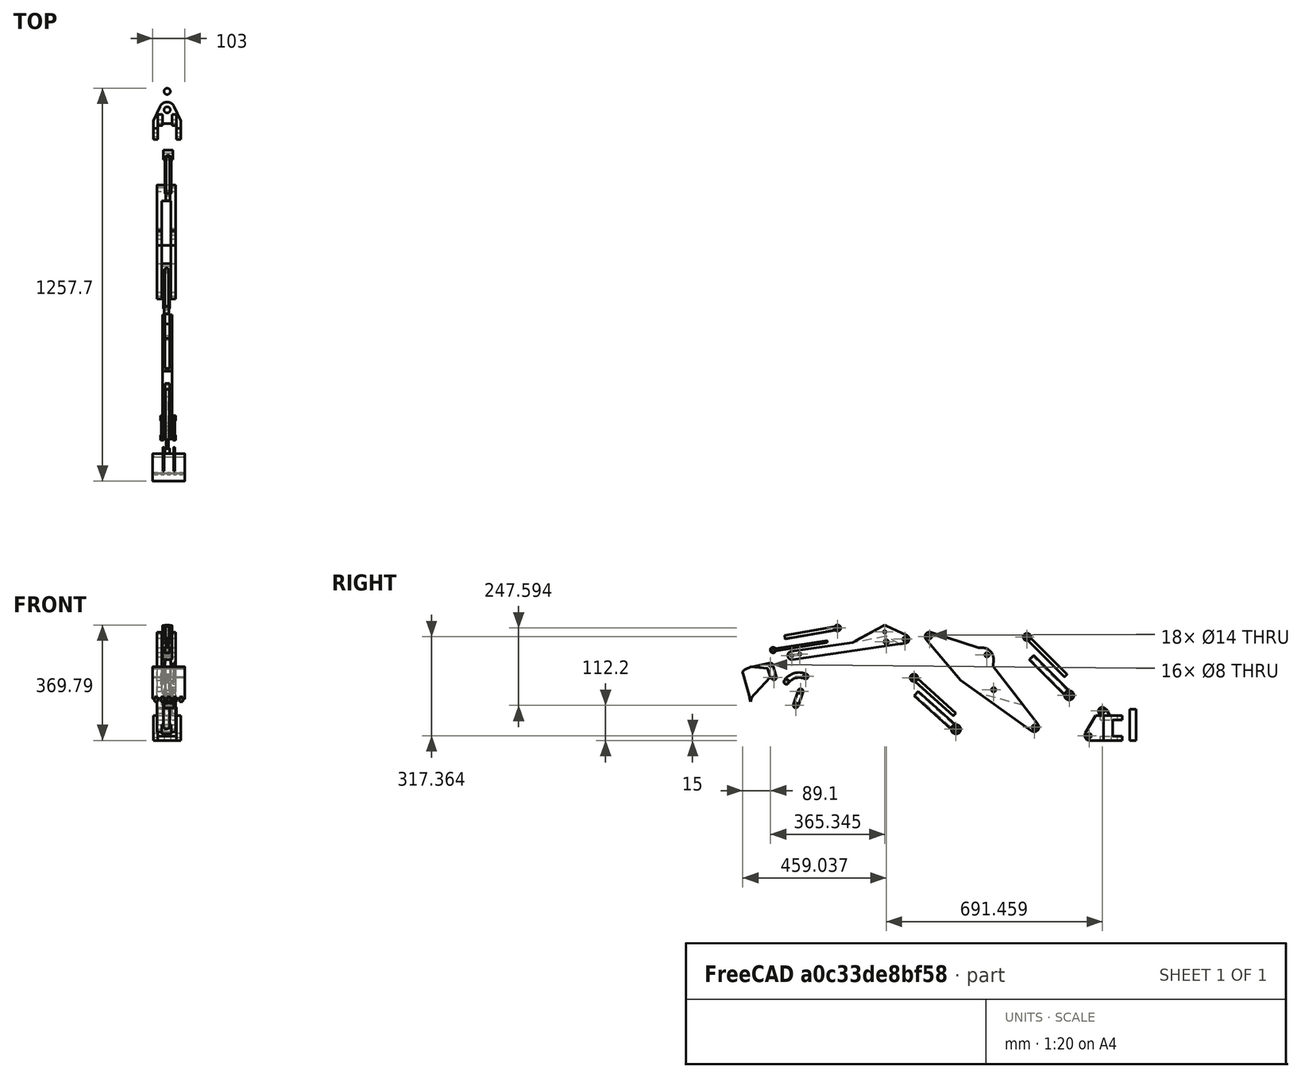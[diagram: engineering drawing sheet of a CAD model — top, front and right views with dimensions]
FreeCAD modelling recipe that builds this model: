
FCSTD DOCUMENT  (FreeCAD 1.2R20260113 (Git shallow))
Label: AssemblyExample
License: CC-BY 4.0
LicenseURL: https://creativecommons.org/licenses/by/4.0/
objects: App::FeaturePython×17, Part::Feature×13, App::Link×13, App::DocumentObjectGroup×1, Assembly::JointGroup×1, Assembly::AssemblyObject×1, App::Point×1
note: 13 computed .brp shape members not serialized (recipe doc carries the construction recipe); baked Part::Feature solids carry a one-line shape summary decoded from their .brp

FEATURE [Part::Feature] Shape001  label="Base"
  shape: bbox 88 x 119.5 x 106 mm, 44 faces (baked)
FEATURE [Part::Feature] Shape012  label="BasePin"
  shape: bbox 20 x 20 x 100 mm, 3 faces (baked)
FEATURE [Part::Feature] Shape013  label="Stick"
  shape: bbox 30 x 388.4 x 109.8 mm, 24 faces (baked)
FEATURE [Part::Feature] Shape014  label="BucketLink1"
  shape: bbox 30 x 31.36 x 61.47 mm, 22 faces (baked)
FEATURE [Part::Feature] Shape015  label="Bucket"
  shape: bbox 103 x 108.6 x 124 mm, 97 faces (baked)
FEATURE [Part::Feature] Shape016  label="BoomCylinderInner"
  shape: bbox 15 x 140.2 x 140.2 mm, 6 faces (baked)
FEATURE [Part::Feature] Shape017  label="StickCylinderInner"
  shape: bbox 15 x 146.3 x 133.8 mm, 6 faces (baked)
FEATURE [Part::Feature] Shape018  label="BucketCylinderInner"
  shape: bbox 15 x 182.7 x 39.88 mm, 6 faces (baked)
FEATURE [Part::Feature] Shape019  label="BucketLink2"
  shape: bbox 48 x 78 x 37.57 mm, 23 faces (baked)
FEATURE [Part::Feature] Shape020  label="BoomCylinderOuter"
  shape: bbox 30 x 143 x 143 mm, 8 faces (baked)
FEATURE [Part::Feature] Shape021  label="StickCylinderOuter"
  shape: bbox 30 x 148.8 x 136.9 mm, 8 faces (baked)
FEATURE [Part::Feature] Shape022  label="BucketCylinderOuter"
  shape: bbox 15 x 179.4 x 45.6 mm, 10 faces (baked)
FEATURE [Part::Feature] Shape  label="Boom"
  shape: bbox 60 x 364 x 319 mm, 31 faces (baked)
FEATURE [App::DocumentObjectGroup] Group  label="CAD"
  Group = -> [Shape001,Shape012,Shape013,Shape014,Shape015,Shape016,Shape017,Shape018,Shape019,Shape020,Shape021,Shape022,Shape]
FEATURE [App::Link] BasePin  label="BasePin001"
  LinkPlacement = pos=(-206.517,40.2557,364.268) rot=(0,0,1;0rad)
  LinkedObject = -> Shape012
  Placement = pos=(-206.517,40.2557,364.268) rot=(0,0,1;0rad)
FEATURE [App::Link] Base  label="Base001"
  LinkPlacement = pos=(-206.517,99.4157,364.268) rot=(0,0,-1;0.004633rad)
  LinkedObject = -> Shape001
  Placement = pos=(-206.517,99.4157,364.268) rot=(0,0,-1;0.004633rad)
FEATURE [App::Link] Boom  label="Boom001"
  LinkPlacement = pos=(-202.932,230.97,229.247) rot=(-0.999947,0.002316,-0.010058;0.452746rad)
  LinkedObject = -> Shape
  Placement = pos=(-202.932,230.97,229.247) rot=(-0.999947,0.002316,-0.010058;0.452746rad)
FEATURE [App::Link] Stick  label="Stick001"
  LinkPlacement = pos=(-205.469,390.408,208.421) rot=(-0.999934,0.002316,-0.011244;0.406359rad)
  LinkedObject = -> Shape013
  Placement = pos=(-205.469,390.408,208.421) rot=(-0.999934,0.002316,-0.011244;0.406359rad)
FEATURE [App::Link] Bucket  label="Bucket001"
  LinkPlacement = pos=(-210.075,432.194,196.62) rot=(-0.99995,0.002316,-0.009747;0.466683rad)
  LinkedObject = -> Shape015
  Placement = pos=(-210.075,432.194,196.62) rot=(-0.99995,0.002316,-0.009747;0.466683rad)
FEATURE [App::Link] BucketLink2  label="BucketLink003"
  LinkPlacement = pos=(-215.535,-1246.73,276.477) rot=(0.999997,-0.002316,0.001009;3.9632rad)
  LinkedObject = -> Shape019
  Placement = pos=(-215.535,-1246.73,276.477) rot=(0.999997,-0.002316,0.001009;3.9632rad)
FEATURE [App::Link] BucketLink1  label="BucketLink004"
  LinkPlacement = pos=(-212.089,-2.4321,-20.3863) rot=(-0.999989,0.002316,-0.004149;1.01849rad)
  LinkedObject = -> Shape014
  Placement = pos=(-212.089,-2.4321,-20.3863) rot=(-0.999989,0.002316,-0.004149;1.01849rad)
FEATURE [App::Link] BoomCylinderOuter  label="BoomCylinderOuter001"
  LinkPlacement = pos=(-209.106,136.254,268.963) rot=(-0.999935,0.002316,-0.011152;0.409629rad)
  LinkedObject = -> Shape020
  Placement = pos=(-209.106,136.254,268.963) rot=(-0.999935,0.002316,-0.011152;0.409629rad)
FEATURE [App::Link] BoomCylinderInner  label="BoomCylinderInner001"
  LinkPlacement = pos=(-208.727,108.582,238.805) rot=(-0.999935,0.002316,-0.011152;0.409629rad)
  LinkedObject = -> Shape016
  Placement = pos=(-208.727,108.582,238.805) rot=(-0.999935,0.002316,-0.011152;0.409629rad)
FEATURE [App::Link] StickCylinderInner  label="StickCylinderInner001"
  LinkPlacement = pos=(-203.709,310.952,236.711) rot=(-0.999971,0.002316,-0.007276;0.616456rad)
  LinkedObject = -> Shape017
  Placement = pos=(-203.709,310.952,236.711) rot=(-0.999971,0.002316,-0.007276;0.616456rad)
FEATURE [App::Link] StickCylinderOuter  label="StickCylinderOuter001"
  LinkPlacement = pos=(-203.027,347.623,221.922) rot=(-0.999971,0.002316,-0.007276;0.616456rad)
  LinkedObject = -> Shape021
  Placement = pos=(-203.027,347.623,221.922) rot=(-0.999971,0.002316,-0.007276;0.616456rad)
FEATURE [App::Link] BucketCylinderInner  label="BucketCylinderInner001"
  LinkPlacement = pos=(-205.355,395.972,110.555) rot=(-0.999962,0.002316,-0.008436;0.535995rad)
  LinkedObject = -> Shape018
  Placement = pos=(-205.355,395.972,110.555) rot=(-0.999962,0.002316,-0.008436;0.535995rad)
FEATURE [App::Link] BucketCylinderOuter  label="BucketCylinderOuter001"
  LinkPlacement = pos=(-205.403,417.48,46.5045) rot=(-0.999964,0.002316,-0.008156;0.553448rad)
  LinkedObject = -> Shape022
  Placement = pos=(-205.403,417.48,46.5045) rot=(-0.999964,0.002316,-0.008156;0.553448rad)
FEATURE [App::FeaturePython] GroundedJoint  # Assembly grounded joint (typed FeaturePython)
  ObjectToGround = -> BasePin
  Placement = pos=(-206.517,40.2557,364.268) rot=(0,0,1;0rad)
FEATURE [App::FeaturePython] Revolute  # Assembly joint (typed FeaturePython)
  Angle = 0
  AngleMax = 0
  AngleMin = 0
  Detach1 = false
  Detach2 = false
  Distance = 0
  Distance2 = 0
  EnableAngleMax = false
  EnableAngleMin = false
  EnableLengthMax = false
  EnableLengthMin = false
  JointType = 1 (Revolute)
  LengthMax = 0
  LengthMin = 0
  Placement1 = pos=(0,59.16,0) rot=(0,0,1;1.5708rad)
  Placement2 = pos=(0,0,0) rot=(0.707107,0.707107,0;3.14159rad)
  Reference1 = -> Assembly [BasePin.Face1,BasePin.Edge2]
  Reference2 = -> Assembly [Base.Edge107,Base.Edge107]
  Suppressed = false
FEATURE [App::FeaturePython] Revolute001  # Assembly joint (typed FeaturePython)
  Angle = 0
  AngleMax = 45
  AngleMin = -45
  Detach1 = false
  Detach2 = false
  Distance = 0
  Distance2 = 0
  EnableAngleMax = true
  EnableAngleMin = true
  EnableLengthMax = false
  EnableLengthMin = false
  JointType = 1 (Revolute)
  LengthMax = 0
  LengthMin = 0
  Placement1 = pos=(-32.9758,-255.877,42.3644) rot=(0.57735,0.57735,0.57735;2.0944rad)
  Placement2 = pos=(-30,-80,15) rot=(-0.57735,-0.57735,0.57735;2.0944rad)
  Reference1 = -> Assembly [Boom.Face1,Boom.Edge5]
  Reference2 = -> Assembly [Base.Edge61,Base.Edge61]
  Suppressed = false
FEATURE [App::FeaturePython] Revolute002  # Assembly joint (typed FeaturePython)
  Angle = 0
  AngleMax = 0
  AngleMin = 0
  Detach1 = false
  Detach2 = false
  Distance = 0
  Distance2 = 0
  EnableAngleMax = false
  EnableAngleMin = false
  EnableLengthMax = false
  EnableLengthMin = false
  JointType = 1 (Revolute)
  LengthMax = 0
  LengthMin = 0
  Placement1 = pos=(-12.24,-144.25,144.25) rot=(0.678598,0.281085,0.678598;2.59356rad)
  Placement2 = pos=(-15,-38.0444,94.4593) rot=(0.57735,-0.57735,0.57735;4.18879rad)
  Reference1 = -> Assembly [BoomCylinderOuter.Edge8,BoomCylinderOuter.Edge8]
  Reference2 = -> Assembly [Base.Edge34,Base.Edge34]
  Suppressed = false
FEATURE [App::FeaturePython] Slider  # Assembly joint (typed FeaturePython)
  Angle = 0
  AngleMax = 0
  AngleMin = 0
  Detach1 = false
  Detach2 = false
  Distance = 0
  Distance2 = 0
  EnableAngleMax = false
  EnableAngleMin = false
  EnableLengthMax = true
  EnableLengthMin = false
  JointType = 3 (Slider)
  LengthMax = 80
  LengthMin = 52.0086
  Placement1 = pos=(2.252,-213.159,265.212) rot=(0,-0.382683,0.92388;3.14159rad)
  Placement2 = pos=(2.76,-265.165,265.165) rot=(0,-0.382683,0.92388;3.14159rad)
  Reference1 = -> Assembly [BoomCylinderInner.Face1,BoomCylinderInner.Face1]
  Reference2 = -> Assembly [BoomCylinderOuter.Face1,BoomCylinderOuter.Edge3]
  Suppressed = false
FEATURE [App::FeaturePython] Cylindrical  # Assembly joint (typed FeaturePython)
  Angle = 0
  AngleMax = 0
  AngleMin = 0
  Detach1 = false
  Detach2 = false
  Distance = 0
  Distance2 = 0
  EnableAngleMax = false
  EnableAngleMin = false
  EnableLengthMax = false
  EnableLengthMin = false
  JointType = 2 (Cylindrical)
  LengthMax = 0
  LengthMin = 0
  Placement1 = pos=(-5.248,-279.1,331.153) rot=(0.678598,-0.281085,0.678598;3.68962rad)
  Placement2 = pos=(-17.9758,-407.377,273.864) rot=(0.57735,0.57735,-0.57735;4.18879rad)
  Reference1 = -> Assembly [BoomCylinderInner.Edge7,BoomCylinderInner.Edge7]
  Reference2 = -> Assembly [Boom.Edge53,Boom.Edge53]
  Suppressed = false
FEATURE [App::FeaturePython] Revolute003  # Assembly joint (typed FeaturePython)
  Angle = 0
  AngleMax = -23
  AngleMin = -48
  Detach1 = false
  Detach2 = false
  Distance = 0
  Distance2 = 0
  EnableAngleMax = true
  EnableAngleMin = true
  EnableLengthMax = false
  EnableLengthMin = false
  JointType = 1 (Revolute)
  LengthMax = 0
  LengthMin = 0
  Placement1 = pos=(12.66,-506.596,35.8372) rot=(0.682415,0.261954,0.682415;2.6292rad)
  Placement2 = pos=(12.0242,-385.877,162.364) rot=(0.57735,0.57735,-0.57735;4.18879rad)
  Reference1 = -> Assembly [StickCylinderOuter.Face2,StickCylinderOuter.Edge3]
  Reference2 = -> Assembly [Boom.Edge66,Boom.Edge66]
  Suppressed = false
FEATURE [App::FeaturePython] Slider001  # Assembly joint (typed FeaturePython)
  Angle = 0
  AngleMax = 0
  AngleMin = 0
  Detach1 = false
  Detach2 = false
  Distance = 0
  Distance2 = 0
  EnableAngleMax = false
  EnableAngleMin = false
  EnableLengthMax = true
  EnableLengthMin = false
  JointType = 3 (Slider)
  LengthMax = 80
  LengthMin = 63.2772
  Placement1 = pos=(-1.828,-571.574,138.121) rot=(0,-0.406737,0.913545;3.14159rad)
  Placement2 = pos=(-2.34,-633.674,150.259) rot=(0,-0.406737,0.913545;3.14159rad)
  Reference1 = -> Assembly [StickCylinderInner.Face1,StickCylinderInner.Face1]
  Reference2 = -> Assembly [StickCylinderOuter.Face6,StickCylinderOuter.Edge3]
  Suppressed = false
FEATURE [App::FeaturePython] Revolute004  # Assembly joint (typed FeaturePython)
  Angle = 0
  AngleMax = 0
  AngleMin = 0
  Detach1 = false
  Detach2 = false
  Distance = 0
  Distance2 = 0
  EnableAngleMax = false
  EnableAngleMin = false
  EnableLengthMax = false
  EnableLengthMin = false
  JointType = 1 (Revolute)
  LengthMax = 0
  LengthMin = 0
  Placement1 = pos=(-14.7,-729.503,315.527) rot=(0.363936,0.85738,0.363936;1.72407rad)
  Placement2 = pos=(-17.9758,-590.877,332.364) rot=(0.57735,0.57735,-0.57735;4.18879rad)
  Reference1 = -> Assembly [Stick.Edge41,Stick.Edge41]
  Reference2 = -> Assembly [Boom.Edge51,Boom.Edge51]
  Suppressed = false
FEATURE [App::FeaturePython] Cylindrical001  # Assembly joint (typed FeaturePython)
  Angle = 0
  AngleMax = 0
  AngleMin = 0
  Detach1 = false
  Detach2 = false
  Distance = 0
  Distance2 = 0
  EnableAngleMax = false
  EnableAngleMin = false
  EnableLengthMax = false
  EnableLengthMin = false
  JointType = 2 (Cylindrical)
  LengthMax = 0
  LengthMin = 0
  Placement1 = pos=(-7.2,-669.12,324.36) rot=(0.363936,0.85738,0.363936;1.72407rad)
  Placement2 = pos=(-9.328,-640.876,200.52) rot=(0.674471,-0.300294,0.674471;3.72505rad)
  Reference1 = -> Assembly [Stick.Edge57,Stick.Edge57]
  Reference2 = -> Assembly [StickCylinderInner.Face4,StickCylinderInner.Face4]
  Suppressed = false
FEATURE [App::FeaturePython] Revolute005  # Assembly joint (typed FeaturePython)
  Angle = 0
  AngleMax = -120
  AngleMin = -145
  Detach1 = false
  Detach2 = false
  Distance = 0
  Distance2 = 0
  EnableAngleMax = true
  EnableAngleMin = true
  EnableLengthMax = false
  EnableLengthMin = false
  JointType = 1 (Revolute)
  LengthMax = 0
  LengthMin = 0
  Placement1 = pos=(-7.14,-885.253,359.794) rot=(0.705758,-0.061746,0.705758;3.26493rad)
  Placement2 = pos=(-7.2,-734.095,347.625) rot=(0.363936,0.85738,0.363936;1.72407rad)
  Reference1 = -> Assembly [BucketCylinderOuter.Face6,BucketCylinderOuter.Face6]
  Reference2 = -> Assembly [Stick.Edge56,Stick.Edge56]
  Suppressed = false
FEATURE [App::FeaturePython] Slider002  # Assembly joint (typed FeaturePython)
  Angle = 0
  AngleMax = 0
  AngleMin = 0
  Detach1 = false
  Detach2 = false
  Distance = 0
  Distance2 = 0
  EnableAngleMax = false
  EnableAngleMin = false
  EnableLengthMax = true
  EnableLengthMin = false
  JointType = 3 (Slider)
  LengthMax = 0
  LengthMin = 0
  Placement1 = pos=(0.212,-1000.72,303.69) rot=(0,-0.760406,0.649448;3.14159rad)
  Placement2 = pos=(0.36,-974.049,344.137) rot=(0,-0.766044,0.642788;3.14159rad)
  Reference1 = -> Assembly [BucketCylinderInner.Face1,BucketCylinderInner.Face1]
  Reference2 = -> Assembly [BucketCylinderOuter.Face1,BucketCylinderOuter.Face1]
  Suppressed = false
FEATURE [App::FeaturePython] Revolute006  # Assembly joint (typed FeaturePython)
  Angle = 0
  AngleMax = 0
  AngleMin = 0
  Detach1 = false
  Detach2 = false
  Distance = 0
  Distance2 = 0
  EnableAngleMax = false
  EnableAngleMin = false
  EnableLengthMax = false
  EnableLengthMin = false
  JointType = 1 (Revolute)
  LengthMax = 0
  LengthMin = 0
  Placement1 = pos=(-12.2189,-987.052,204.816) rot=(-0.707107,0,-0.707107;3.14159rad)
  Placement2 = pos=(-14.7,-1006.04,276.188) rot=(0.363936,0.85738,0.363936;1.72407rad)
  Reference1 = -> Assembly [BucketLink2.Edge49,BucketLink2.Edge49]
  Reference2 = -> Assembly [Stick.Face20,Stick.Edge10]
  Suppressed = false
FEATURE [App::FeaturePython] Revolute007  # Assembly joint (typed FeaturePython)
  Angle = 0
  AngleMax = 0
  AngleMin = 0
  Detach1 = false
  Detach2 = false
  Distance = 0
  Distance2 = 0
  EnableAngleMax = false
  EnableAngleMin = false
  EnableLengthMax = false
  EnableLengthMin = false
  JointType = 1 (Revolute)
  LengthMax = 0
  LengthMin = 0
  Placement1 = pos=(-9.9,-1088.34,200.94) rot=(0.57735,0.57735,0.57735;2.0944rad)
  Placement2 = pos=(-14.7,-1031.22,271.858) rot=(0.363936,0.85738,0.363936;1.72407rad)
  Reference1 = -> Assembly [Bucket.Edge139,Bucket.Edge139]
  Reference2 = -> Assembly [Stick.Face20,Stick.Edge6]
  Suppressed = false
FEATURE [App::FeaturePython] Revolute008  # Assembly joint (typed FeaturePython)
  Angle = 0
  AngleMax = 0
  AngleMin = 0
  Detach1 = false
  Detach2 = false
  Distance = 0
  Distance2 = 0
  EnableAngleMax = false
  EnableAngleMin = false
  EnableLengthMax = false
  EnableLengthMin = false
  JointType = 1 (Revolute)
  LengthMax = 0
  LengthMin = 0
  Placement1 = pos=(-9.9,-1018.98,112.2) rot=(0.57735,0.57735,0.57735;2.0944rad)
  Placement2 = pos=(-9.9,-1099.44,240.39) rot=(0.57735,0.57735,0.57735;2.0944rad)
  Reference1 = -> Assembly [BucketLink1.Face11,BucketLink1.Face11]
  Reference2 = -> Assembly [Bucket.Face65,Bucket.Edge2]
  Suppressed = false
FEATURE [App::FeaturePython] Cylindrical002  # Assembly joint (typed FeaturePython)
  Angle = 0
  AngleMax = 0
  AngleMin = 0
  Detach1 = false
  Detach2 = false
  Distance = 0
  Distance2 = 0
  EnableAngleMax = false
  EnableAngleMin = false
  EnableLengthMax = false
  EnableLengthMin = false
  JointType = 2 (Cylindrical)
  LengthMax = 0
  LengthMin = 0
  Placement1 = pos=(-2.9,-1003.62,157.675) rot=(0.57735,0.57735,0.57735;2.0944rad)
  Placement2 = pos=(2.78108,-1049.05,187.816) rot=(-0.57735,-0.57735,-0.57735;4.18879rad)
  Reference1 = -> Assembly [BucketLink1.Edge25,BucketLink1.Edge25]
  Reference2 = -> Assembly [BucketLink2.Face13,BucketLink2.Face13]
  Suppressed = false
FEATURE [App::FeaturePython] Cylindrical003  # Assembly joint (typed FeaturePython)
  Angle = 0
  AngleMax = 0
  AngleMin = 0
  Detach1 = false
  Detach2 = false
  Distance = 0
  Distance2 = 0
  EnableAngleMax = false
  EnableAngleMin = false
  EnableLengthMax = false
  EnableLengthMin = false
  JointType = 2 (Cylindrical)
  LengthMax = 0
  LengthMin = 0
  Placement1 = pos=(0.211998,-1091.57,289.302) rot=(0.544663,-0.637718,0.544663;4.27698rad)
  Placement2 = pos=(2.78108,-1049.05,187.816) rot=(-0.57735,-0.57735,-0.57735;4.18879rad)
  Reference1 = -> Assembly [BucketCylinderInner.Face3,BucketCylinderInner.Face3]
  Reference2 = -> Assembly [BucketLink2.Face13,BucketLink2.Face13]
  Suppressed = false
FEATURE [Assembly::JointGroup] Joints
  Group = -> [GroundedJoint,Revolute,Revolute001,Revolute002,Slider,Cylindrical,Revolute003,Slider001,Revolute004,Cylindrical001,Revolute005,Slider002,Revolute006,Revolute007,Revolute008,Cylindrical002,Cylindrical003]
FEATURE [Assembly::AssemblyObject] Assembly
  Group = -> [Joints,BasePin,Base,Boom,Stick,Bucket,BucketLink2,BucketLink1,BoomCylinderOuter,BoomCylinderInner,StickCylinderInner,StickCylinderOuter,BucketCylinderInner,BucketCylinderOuter,GroundedJoint,Revolute,Revolute001,Revolute002,Slider,Cylindrical,Revolute003,Slider001,Revolute004,Cylindrical001,Revolute005,Slider002,Revolute006,Revolute007,Revolute008,Cylindrical002,Cylindrical003]
  Origin = -> Origin
  Type = Assembly
FEATURE [App::Point] Origin001  label="Ursprung"
  Role = Origin
